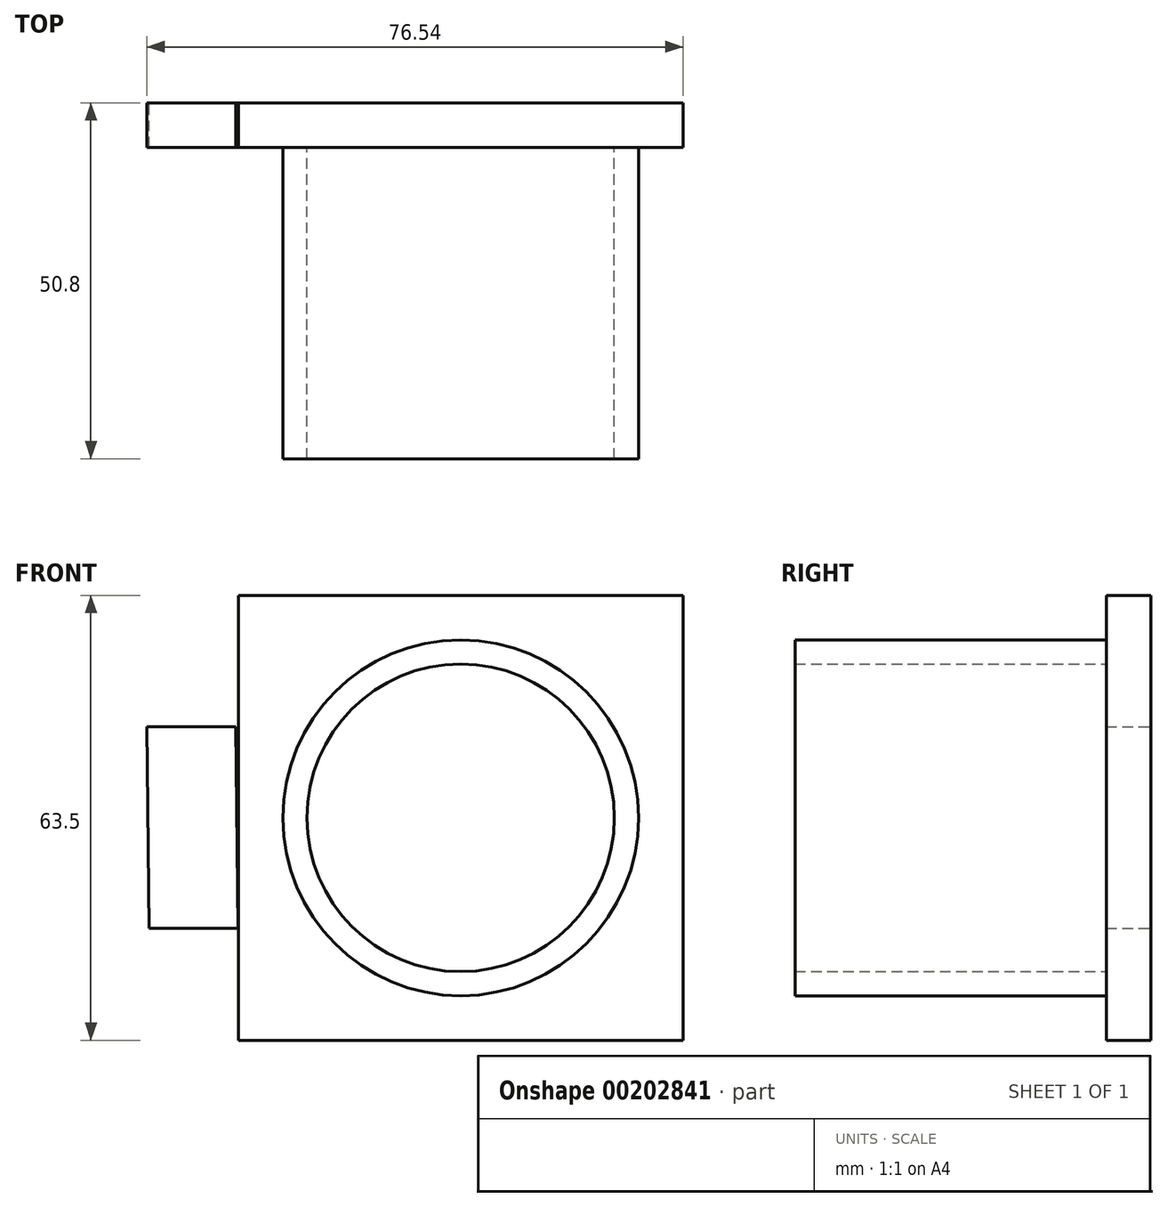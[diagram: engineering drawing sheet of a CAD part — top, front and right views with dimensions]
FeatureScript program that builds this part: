
annotation { "Feature Type Name" : "Feature", "Feature Type Description" : "" }
export const myFeature = defineFeature(function(context is Context, id is Id, definition is map)
    precondition{}
    {
        {
            var Q0;
            Q0=qCreatedBy(makeId("Front.planeOp"),FACE);
            var sketch = newSketch(context, id + "F0", { "sketchPlane" : qUnion([Q0])});
            skCircle(sketch, "E0", {"center": v(0, 0) * mm, "radius": 25.4 * mm});
            skCircle(sketch, "E1", {"center": v(0, 0) * mm, "radius": 21.95 * mm});
            skSolve(sketch);
        }
        {
            var Q0;
            Q0 = qSketchRegion(id + "F0", true);
            extrude(context, id + "F1", {"entities" : qUnion([Q0]), "depth" : 50.8 * mm});
        }
        {
            var Q0;
            Q0=makeQuery(id+"F0.imprint","IMPRINT",FACE,{"disambiguationData":[TD([[makeQuery(id+"F0.imprint","IMPRINT",EDGE,{"derivedFrom":sQuery(id+"F0.wireOp",EDGE,"E1")}),1.0]])]});
            extrude(context, id + "F2", {"entities" : qUnion([Q0]), "operationType" : NewBodyOperationType.REMOVE, "endBound" : BoundingType.THROUGH_ALL, "oppositeDirection" : true, "depth" : 25.4 * mm});
        }
        {
            var Q0;
            Q0=qCreatedBy(makeId("Front.planeOp"),FACE);
            var sketch = newSketch(context, id + "F3", { "sketchPlane" : qUnion([Q0])});
            skLineSegment(sketch, "E2", {"start": v(-18.07, 8.1) * mm, "end": v(18.18, -7.74) * mm, "construction": true});
            skLineSegment(sketch, "E3.bottom", {"start": v(-31.75, -31.75) * mm, "end": v(31.75, -31.75) * mm});
            skLineSegment(sketch, "E3.top", {"start": v(-31.75, 31.75) * mm, "end": v(31.75, 31.75) * mm});
            skLineSegment(sketch, "E3.left", {"start": v(-31.75, -31.75) * mm, "end": v(-31.75, 31.75) * mm});
            skLineSegment(sketch, "E3.right", {"start": v(31.75, -31.75) * mm, "end": v(31.75, 31.75) * mm});
            skPoint(sketch, "E3.middle", {"position": v(0, 0) * mm});
            skSolve(sketch);
        }
        {
            var Q0;
            Q0 = qSketchRegion(id + "F3", true);
            extrude(context, id + "F4", {"entities" : qUnion([Q0]), "operationType" : NewBodyOperationType.ADD, "depth" : 6.35 * mm});
        }
        {
            var Q0;
            Q0=qCreatedBy(makeId("Front.planeOp"),FACE);
            var sketch = newSketch(context, id + "F5", { "sketchPlane" : qUnion([Q0])});
            skLineSegment(sketch, "E4", {"start": v(-32.09, 13.01) * mm, "end": v(-44.79, 13.01) * mm});
            skLineSegment(sketch, "E5", {"start": v(-31.8, -15.75) * mm, "end": v(-44.5, -15.75) * mm});
            skLineSegment(sketch, "E6", {"start": v(-44.79, 13.01) * mm, "end": v(-44.5, -15.75) * mm});
            skLineSegment(sketch, "E7", {"start": v(-32.09, 13.01) * mm, "end": v(-31.8, -15.75) * mm});
            skSolve(sketch);
        }
        {
            var Q0;
            Q0=makeQuery(id+"F5.imprint","IMPRINT",FACE,{"disambiguationData":[TD([[makeQuery(id+"F5.imprint","IMPRINT",EDGE,{"derivedFrom":sQuery(id+"F5.wireOp",EDGE,"E4")}),1.0]])]});
            extrude(context, id + "F6", {"entities" : qUnion([Q0]), "depth" : 6.35 * mm});
        }
    });
